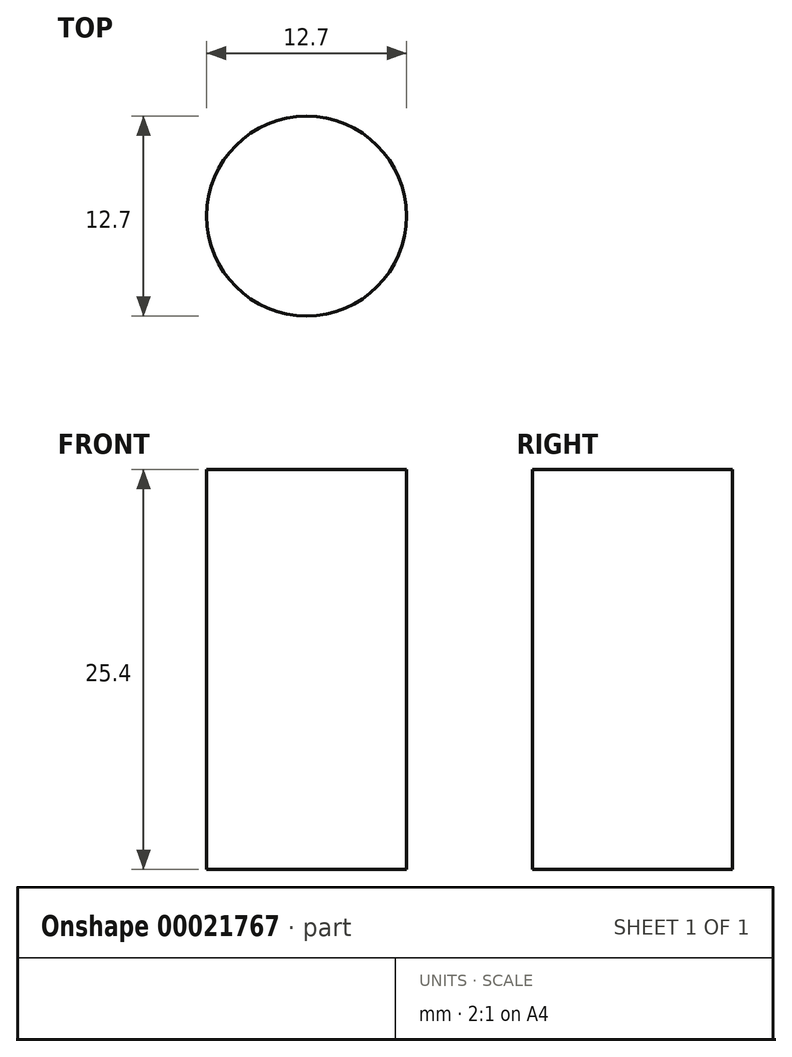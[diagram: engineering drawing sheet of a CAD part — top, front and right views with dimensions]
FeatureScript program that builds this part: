
annotation { "Feature Type Name" : "Feature", "Feature Type Description" : "" }
export const myFeature = defineFeature(function(context is Context, id is Id, definition is map)
    precondition{}
    {
        {
            var Q0;
            Q0=qCreatedBy(makeId("Top.planeOp"),FACE);
            var sketch = newSketch(context, id + "F0", { "sketchPlane" : qUnion([Q0])});
            skCircle(sketch, "E0", {"center": v(0, 0) * mm, "radius": 6.35 * mm});
            skSolve(sketch);
        }
        {
            var Q0;
            Q0=makeQuery(id+"F0.imprint","IMPRINT",FACE,{"disambiguationData":[TD([[makeQuery(id+"F0.imprint","IMPRINT",EDGE,{"derivedFrom":sQuery(id+"F0.wireOp",EDGE,"E0")}),1.0]])]});
            extrude(context, id + "F1", {"entities" : qUnion([Q0]), "depth" : 25.4 * mm});
        }
    });
